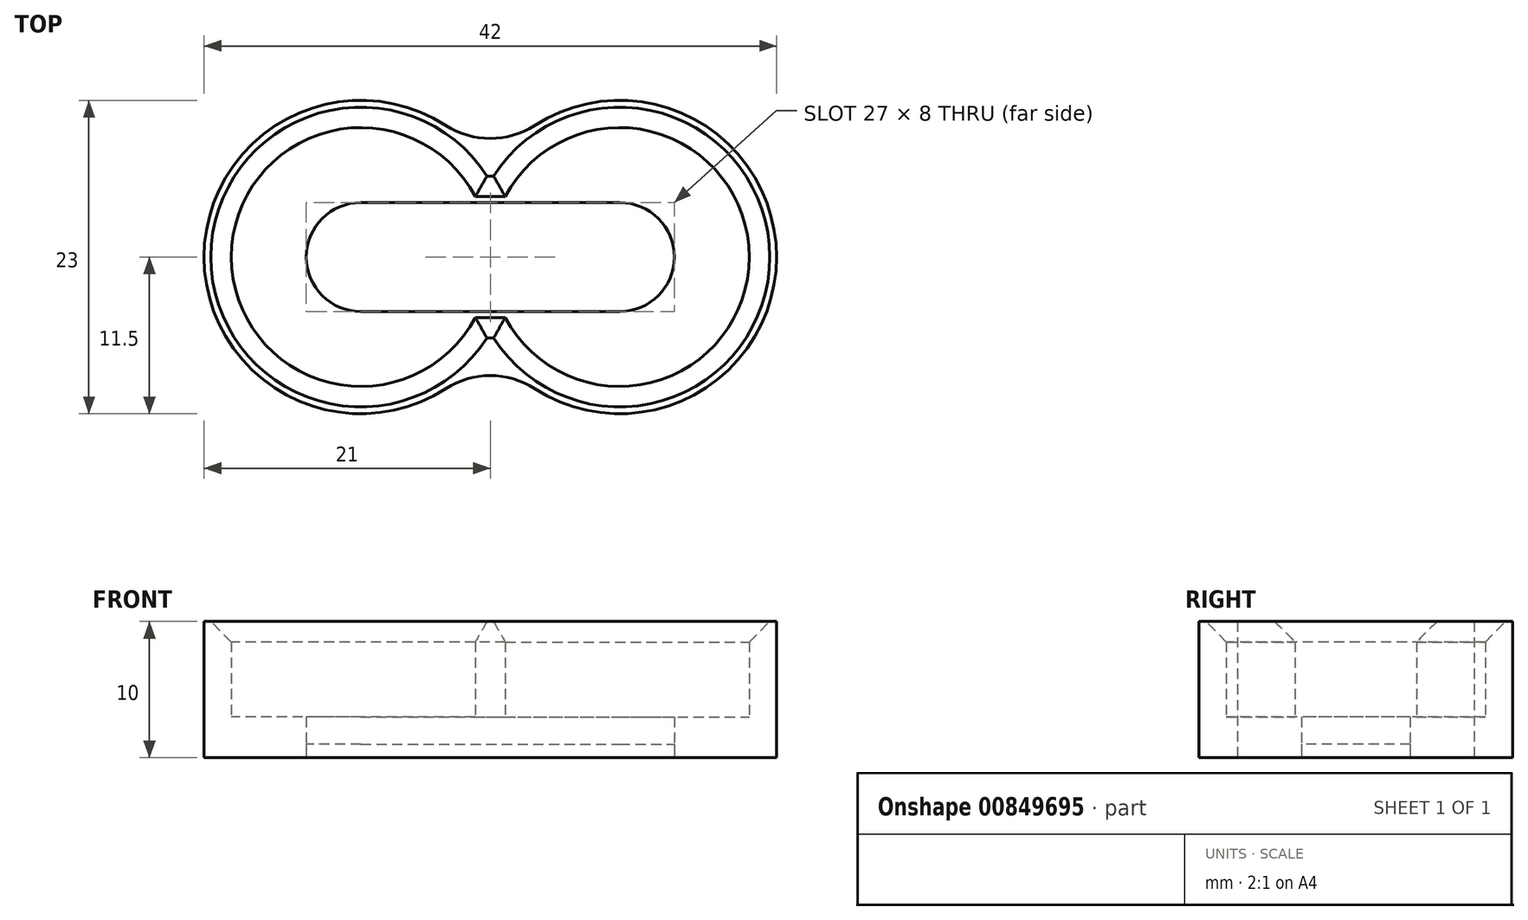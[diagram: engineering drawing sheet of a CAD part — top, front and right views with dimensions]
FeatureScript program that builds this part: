
annotation { "Feature Type Name" : "Feature", "Feature Type Description" : "" }
export const myFeature = defineFeature(function(context is Context, id is Id, definition is map)
    precondition{}
    {
        {
            var Q0;
            Q0=qCreatedBy(makeId("Top.planeOp"),FACE);
            var sketch = newSketch(context, id + "F0", { "sketchPlane" : qUnion([Q0])});
            skArc(sketch, "E0", {"start": v(0, 4) * mm, "mid": v(-4, 0) * mm, "end": v(0, -4) * mm});
            skArc(sketch, "E1", {"start": v(8.4, 4.45) * mm, "mid": v(-9.5, 0) * mm, "end": v(8.4, -4.45) * mm});
            skArc(sketch, "E2", {"start": v(6.24, 9.66) * mm, "mid": v(-11.5, 0) * mm, "end": v(6.24, -9.66) * mm});
            skLineSegment(sketch, "E3", {"start": v(9.5, 19.95) * mm, "end": v(9.5, -22.09) * mm, "construction": true});
            skArc(sketch, "E4.MirrorC", {"start": v(12.76, 9.66) * mm, "mid": v(30.5, 0) * mm, "end": v(12.76, -9.66) * mm});
            skArc(sketch, "E5.MirrorC", {"start": v(10.6, 4.45) * mm, "mid": v(28.5, 0) * mm, "end": v(10.6, -4.45) * mm});
            skArc(sketch, "E6.MirrorC", {"start": v(19, 4) * mm, "mid": v(23, 0) * mm, "end": v(19, -4) * mm});
            skLineSegment(sketch, "E7", {"start": v(8.4, 4.45) * mm, "end": v(10.6, 4.45) * mm});
            skLineSegment(sketch, "E8", {"start": v(8.4, -4.45) * mm, "end": v(10.6, -4.45) * mm});
            skLineSegment(sketch, "E9", {"start": v(0, 4) * mm, "end": v(19, 4) * mm});
            skLineSegment(sketch, "E10", {"start": v(-18.56, 0) * mm, "end": v(51.26, 0) * mm, "construction": true});
            skLineSegment(sketch, "E11.MirrorCS", {"start": v(0, -4) * mm, "end": v(19, -4) * mm});
            skArc(sketch, "E12", {"start": v(6.24, 9.66) * mm, "mid": v(9.5, 8.7) * mm, "end": v(12.76, 9.66) * mm});
            skArc(sketch, "E13.MirrorC", {"start": v(6.24, -9.66) * mm, "mid": v(9.5, -8.7) * mm, "end": v(12.76, -9.66) * mm});
            skSolve(sketch);
        }
        {
            var Q0;
            Q0=makeQuery(id+"F0.imprint","IMPRINT",FACE,{"disambiguationData":[TD([[makeQuery(id+"F0.imprint","IMPRINT",EDGE,{"derivedFrom":sQuery(id+"F0.wireOp",EDGE,"E0")}),1.0]])]});
            var Q1;
            Q1=makeQuery(id+"F0.imprint","IMPRINT",FACE,{"disambiguationData":[TD([[makeQuery(id+"F0.imprint","IMPRINT",EDGE,{"derivedFrom":sQuery(id+"F0.wireOp",EDGE,"E6.MirrorC")}),-1.0]])]});
            extrude(context, id + "F1", {"entities" : qUnion([Q0, Q1]), "depth" : 1 * mm, "offsetDistance" : 25 * mm});
        }
        {
            var Q0;
            Q0=makeQuery(id+"F0.imprint","IMPRINT",FACE,{"disambiguationData":[TD([[makeQuery(id+"F0.imprint","IMPRINT",EDGE,{"derivedFrom":sQuery(id+"F0.wireOp",EDGE,"E0")}),-1.0]])]});
            extrude(context, id + "F2", {"entities" : qUnion([Q0]), "depth" : 3 * mm, "offsetDistance" : 25 * mm});
        }
        {
            var Q0;
            Q0=makeQuery(id+"F0.imprint","IMPRINT",FACE,{"disambiguationData":[TD([[makeQuery(id+"F0.imprint","IMPRINT",EDGE,{"derivedFrom":sQuery(id+"F0.wireOp",EDGE,"E1")}),-1.0]])]});
            extrude(context, id + "F3", {"entities" : qUnion([Q0]), "operationType" : NewBodyOperationType.ADD, "depth" : 10 * mm, "offsetDistance" : 25 * mm});
        }
        {
            var Q0;
            Q0=makeQuery(id+"F3.opExtrude","CAP_EDGE",EDGE,{"disambiguationData":[OSD([sQuery(id+"F0.wireOp",EDGE,"E1")])],"isStart":false});
            var Q1;
            Q1=makeQuery(id+"F3.opExtrude","CAP_EDGE",EDGE,{"disambiguationData":[OSD([sQuery(id+"F0.wireOp",EDGE,"E5.MirrorC")])],"isStart":false});
            var Q2;
            Q2=makeQuery(id+"F3.opExtrude","CAP_EDGE",EDGE,{"disambiguationData":[OSD([sQuery(id+"F0.wireOp",EDGE,"E7")])],"isStart":false});
            var Q3;
            Q3=makeQuery(id+"F3.opExtrude","CAP_EDGE",EDGE,{"disambiguationData":[OSD([sQuery(id+"F0.wireOp",EDGE,"E8")])],"isStart":false});
            chamfer(context, id + "F4", {"entities" : qUnion([Q0, Q1, Q2, Q3]), "width" : 1.5 * mm, "tangentPropagation" : true});
        }
    });
